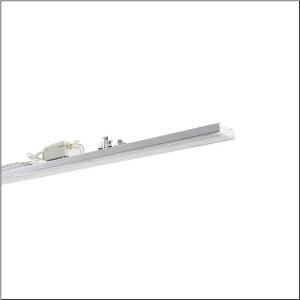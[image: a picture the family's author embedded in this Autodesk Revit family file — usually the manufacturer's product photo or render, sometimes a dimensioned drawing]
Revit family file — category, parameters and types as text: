
# Revit family: licross_r__21_recessed_ho_52te12dn4fxm3c_36c1
name_source: partatom
category: Lighting Fixtures
units: mm (PartAtom-declared; Revit-internal decimal feet)

## family parameters
Cut with Voids When Loaded = No
Host = Face
Light Source = No
Part Type = Normal
Room Calculation Point = No
Round Connector Dimension = Use Diameter
Shared = No

## types (1)
- --- (1 x LED, 930 lm, 7.5 W, 4000K)
    Apparent Load = 8 VA
    CIE Flux Codes = 69 91 98 100 100
    Color Rendering = 80
    Color Temperature = 4000K
    Default Elevation = 1800 mm
    Description = Licross® 21 Recessed HO, luminaire insert, of sheet steel, galvanised, coil coated, white, length: 1.500mm, width: 66mm, height: 67mm, LED rated luminous flux: 15.000lm, light colour: 840, control gear: DALI 2, with plug, 6-pole, with phase selection, for trunking rail, 14-core, mains connection: 220..240V, AC, 50/60Hz, rated input power: 88W, halogen-free wiring, for emergency light function, for trunking rail, 14-core, converter,control gear: single battery element, battery: LiFeP04, 9Ah, primary optical cover: cover, of PMMA, light emission: direct distribution, primary light characteristic: symmetric, protection rating (complete): IP54, insulation class (complete): insulation class I (protective earthing), certification: CE, UKCA, protection symbol: D if used in an environment with non-conductive dust loads with corresponding accessories, impact resistance: IK06, permissible ambient temperature for indoor applications: +5..+30°C, standard: EN 60598-2-22, LABS conformity tested according to VDMA 24364:2018-05, reducing of maximum allowable ambient temperature of 5°C with ceiling mounting, corresponds to IFS (International Featured Standards) requirements for safety and quality in the food industry, packaging unit: 1 piece
    Height = 58 mm
    Lamp = 1 x LED
    Lamp Light Flux = 930 lm
    Lamp Power = 7.5 W
    Lamp count = 1
    Length = 1500 mm
    Luminous efficacy = 124 lm/W
    Manufacturer = Siteco
    ModVariant = No
    Model = 52TE12DN4FXM3C
    Mounting Place = Ceiling
    Mounting Type = Pendant
    Number of Poles = 1
    OnlyDefault = Yes
    Power Factor = 1
    Product Name = Licross® 21 Recessed HO
    Product group = luminaire insert
    ProductGroupID = 901
    Protection Class = Protection class I
    Protection Degree = IP 54
    RLX_Detail_Level = 1
    RLX_Emergency_Light_Flux = 0 lm
    RLX_Emergency_Type = 0
    RLX_Emergency_Type_DB = No
    RlxData = <blob elided: 25133 chars, md5=18339e74>
    Socket = socket
    Standby Power = 0 W
    System Light Flux = 930 lm
    System Power = 8 W
    Type Comments = : emergency light operation: 3 h
    Type Image = l_1296930.jpg
    URL = http://relux.com
    VarID = @adj_039445
    Voltage = 0 V
    Weight = 0.00 kg
    Width = 66 mm

## geometry (parser evidence)
native form markers: Blend x4, Sweep x12
no freeform markers — native parametric forms only
